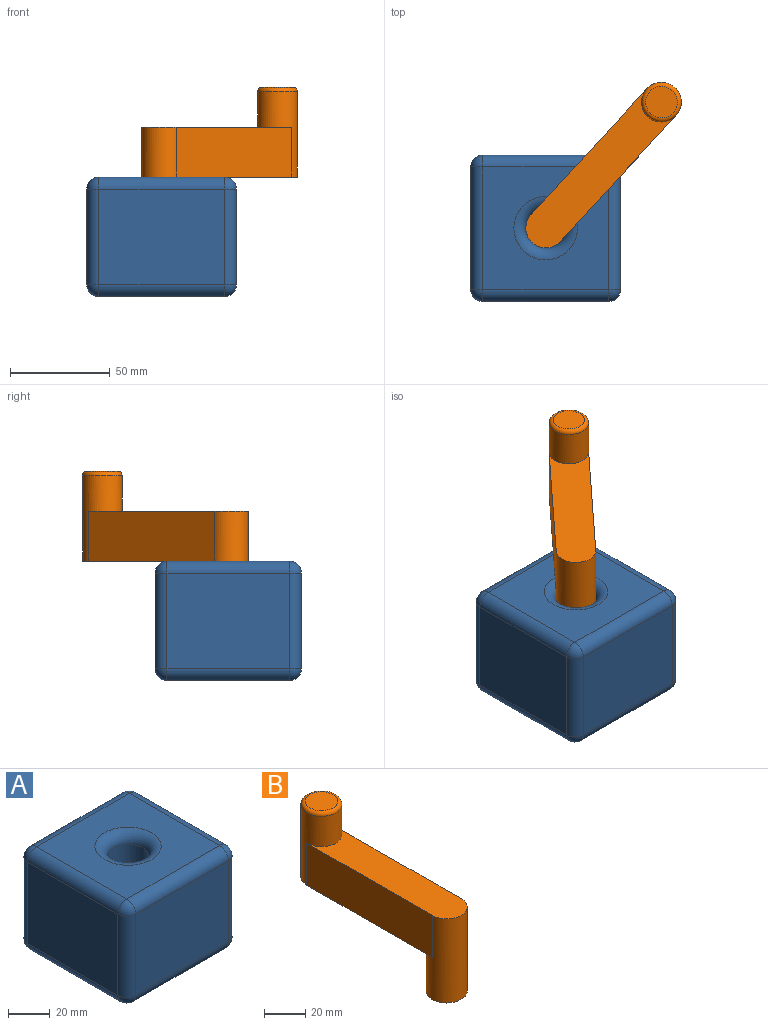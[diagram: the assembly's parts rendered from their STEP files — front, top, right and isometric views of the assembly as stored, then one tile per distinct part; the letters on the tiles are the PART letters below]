
ASSEMBLY  parts=2 mates=1
PART A: 28 faces, bbox 75.2x73.5x60 mm
  f0: plane 63.19x48mm, normal (0,-1,0), area 3033.2mm2, adj f15,f20,f23,f26
  f1: plane 61.54x48mm, normal (1,0,0), area 2954mm2, adj f12,f21,f22,f26
  f2: plane 63.19x48mm, normal (0,1,0), area 3033.2mm2, adj f7,f11,f12,f13
  f3: cylinder r=9.94mm len=54mm, axis (0,0,-1), area 3372.2mm2, adj f6,f27
  f4: plane 61.54x48mm, normal (-1,0,0), area 2954mm2, adj f7,f10,f14,f15
  f5: plane 63.19x61.54mm, normal (0,0,1), area 3090.7mm2, adj f10,f11,f20,f21,f27
  f6: plane 63.19x61.54mm, normal (0,0,-1), area 3578.5mm2, adj f3,f13,f14,f22,f23
  f7: cylinder r=6mm len=48mm, axis (0,0,1), area 452.4mm2, adj f2,f4,f8,f9
  f8: sphere r=6mm, area 56.5mm2, adj f7,f10,f11
  f9: sphere r=6mm, area 56.5mm2, adj f7,f13,f14
  f10: cylinder r=6mm len=61.54mm, axis (0,1,0), area 580mm2, adj f4,f5,f8,f16
  f11: cylinder r=6mm len=63.19mm, axis (1,0,0), area 595.6mm2, adj f2,f5,f8,f17
  f12: cylinder r=6mm len=48mm, axis (0,0,-1), area 452.4mm2, adj f1,f2,f17,f18
  f13: cylinder r=6mm len=63.19mm, axis (-1,0,0), area 595.6mm2, adj f2,f6,f9,f18
  f14: cylinder r=6mm len=61.54mm, axis (0,-1,0), area 580mm2, adj f4,f6,f9,f19
  f15: cylinder r=6mm len=48mm, axis (0,0,-1), area 452.4mm2, adj f0,f4,f16,f19
  f16: sphere r=6mm, area 56.5mm2, adj f10,f15,f20
  f17: sphere r=6mm, area 56.5mm2, adj f11,f12,f21
  f18: sphere r=6mm, area 56.5mm2, adj f12,f13,f22
  f19: sphere r=6mm, area 56.5mm2, adj f14,f15,f23
  f20: cylinder r=6mm len=63.19mm, axis (-1,0,0), area 595.6mm2, adj f0,f5,f16,f24
  f21: cylinder r=6mm len=61.54mm, axis (0,-1,0), area 580mm2, adj f1,f5,f17,f24
  f22: cylinder r=6mm len=61.54mm, axis (0,1,0), area 580mm2, adj f1,f6,f18,f25
  f23: cylinder r=6mm len=63.19mm, axis (1,0,0), area 595.6mm2, adj f0,f6,f19,f25
  f24: sphere r=6mm, area 56.5mm2, adj f20,f21,f26
  f25: sphere r=6mm, area 56.5mm2, adj f22,f23,f26
  f26: cylinder r=6mm len=48mm, axis (0,0,1), area 452.4mm2, adj f0,f1,f24,f25
  f27: torus R=15.94mm, axis (0,0,1), area 717.7mm2, adj f3,f5
PART B: 9 faces, bbox 21.5x106.6x70 mm
  f0: plane 85.92x25mm, normal (-1,0,0), area 2148.1mm2, adj f1,f3,f4,f5
  f1: cylinder r=9.94mm len=50mm, axis (0,0,-1), area 2341.8mm2, adj f0,f2,f4,f5,f6
  f2: plane 85.92x25mm, normal (1,0,0), area 2148.1mm2, adj f1,f3,f4,f5
  f3: cylinder r=9.94mm len=43mm, axis (0,0,-1), area 1904.6mm2, adj f0,f2,f4,f5,f8
  f4: plane 95.86x19.88mm, normal (0,0,1), area 1707.9mm2, adj f0,f1,f2,f3
  f5: plane 95.86x19.88mm, normal (0,0,-1), area 1707.9mm2, adj f0,f1,f2,f3
  f6: plane 19.88x19.88mm, normal (0,0,-1), area 310.3mm2, adj f1
  f7: plane 15.88x15.88mm, normal (0,0,1), area 198mm2, adj f8
  f8: torus R=7.94mm, axis (0,0,1), area 181.8mm2, adj f3,f7
PLACE A t=(-11.37,3.56,-16.62)mm fixed
PLACE B rot(axis=(0,0,-1),42.6deg) t=(-11.37,3.56,-16.62)mm
MATE revolute B.f1 <-> A.f3  axis (0,0,-1) through (-11.37,3.56,43.38)mm
